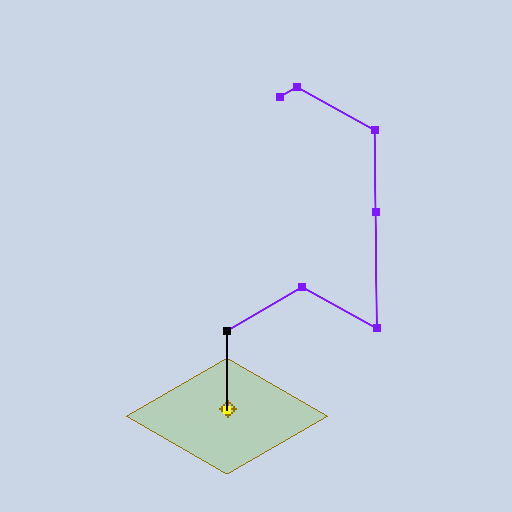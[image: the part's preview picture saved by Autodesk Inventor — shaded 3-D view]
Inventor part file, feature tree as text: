
AUTODESK INVENTOR PART (.ipt)
format: ipt  version: 2025 (Build 290162000, 162)  size: 162,304 bytes
history: native  units: in
note: dims shown in document units (in); Inventor stores cm internally (conversion verified against a paired STEP export)
features: other x1, plane x1, sketch x1
ambient origin geometry x8: Origin, YZ Plane, XZ Plane, XY Plane, X Axis, Y Axis, Z Axis, Center Point
feature tree (3):
  other  "Work Point1"
  plane  "Work Plane1"
  sketch  "3D Sketch1"
